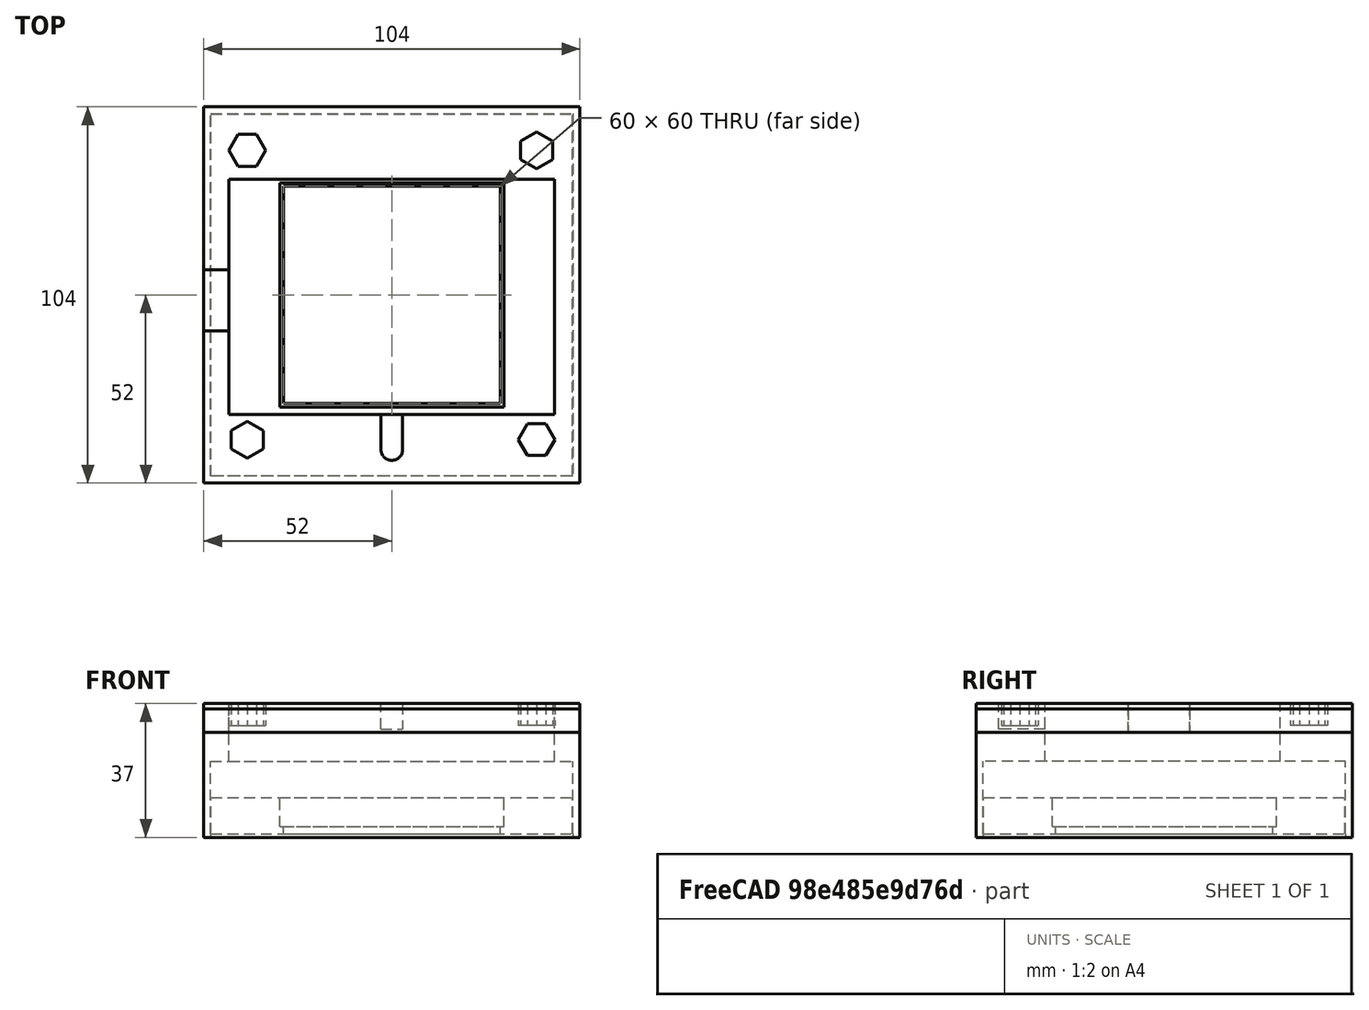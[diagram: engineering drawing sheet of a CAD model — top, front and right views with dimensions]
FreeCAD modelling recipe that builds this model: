
FCSTD DOCUMENT  (FreeCAD 1.0R39319 (Git))
Label: Matrix 3 original cut with switch notch
License: All rights reserved
LicenseURL: https://en.wikipedia.org/wiki/All_rights_reserved
objects: Part::Box×6, Part::Cut×5, Part::MultiFuse×5, Part::Feature×1
note: 17 computed .brp shape members not serialized (recipe doc carries the construction recipe); baked Part::Feature solids carry a one-line shape summary decoded from their .brp

FEATURE [Part::Feature] Part__Feature  label="Box"
  shape: bbox 104 x 104 x 37 mm, 80 faces (baked)
FEATURE [Part::Box] Box  label="Cube"
  AttacherType = Attacher::AttachEngine3D
  Height = 10
  Length = 100
  Placement = pos=(-50,-50,0) rot=(0,0,1;0rad)
  Width = 100
FEATURE [Part::Box] Box001  label="Cube001"
  AttacherType = Attacher::AttachEngine3D
  Height = 10
  Length = 60
  Placement = pos=(-30,-30,0) rot=(0,0,1;0rad)
  Width = 60
FEATURE [Part::Cut] Cut
  Base = -> Box
  Tool = -> Box001
FEATURE [Part::Box] Box002  label="Cube002"
  AttacherType = Attacher::AttachEngine3D
  Height = 8
  Length = 60
  Placement = pos=(-30,-30,2) rot=(0,0,1;0rad)
  Width = 60
FEATURE [Part::MultiFuse] Fusion
  Shapes = -> [Box002,Cut]
FEATURE [Part::Cut] Cut001
  Base = -> Fusion
  Tool = -> Box002
FEATURE [Part::Box] Box003  label="Cube003"
  AttacherType = Attacher::AttachEngine3D
  Height = 8
  Length = 62
  Placement = pos=(-31,-31,2) rot=(0,0,1;0rad)
  Width = 62
FEATURE [Part::MultiFuse] Fusion001
  Shapes = -> [Cut001,Box003]
FEATURE [Part::Cut] Cut002
  Base = -> Fusion001
  Tool = -> Box003
FEATURE [Part::Box] Box004  label="Cube004"
  AttacherType = Attacher::AttachEngine3D
  Height = 29
  Length = 90
  Placement = pos=(-45,-33,12) rot=(0,0,1;0rad)
  Width = 65
FEATURE [Part::MultiFuse] Fusion002
  Shapes = -> [Box004,Cut002]
FEATURE [Part::MultiFuse] Fusion003
  Shapes = -> [Part__Feature,Fusion002,Box004,Cut002]
FEATURE [Part::Cut] Cut003
  Base = -> Fusion003
  Tool = -> Box004
FEATURE [Part::Box] Box005  label="Cube005"
  AttacherType = Attacher::AttachEngine3D
  Height = 8
  Length = 9
  Placement = pos=(-53,-10,28) rot=(0,0,1;0rad)
  Width = 17
FEATURE [Part::MultiFuse] Fusion004
  Shapes = -> [Cut003,Box005]
FEATURE [Part::Cut] Cut004
  Base = -> Fusion004
  Tool = -> Box005
